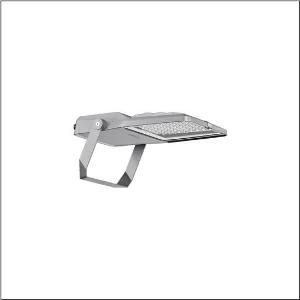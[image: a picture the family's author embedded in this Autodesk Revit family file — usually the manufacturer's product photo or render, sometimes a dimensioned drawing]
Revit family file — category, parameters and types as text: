
# Revit family: floodlight_fl_21_mini___pl64_5xa7776d2e1a_08ea
name_source: partatom
category: Lighting Fixtures
units: mm (PartAtom-declared; Revit-internal decimal feet)

## family parameters
Cut with Voids When Loaded = No
Host = Face
Light Source = No
Part Type = Normal
Room Calculation Point = No
Round Connector Dimension = Use Diameter
Shared = No

## types (1)
- --- (1 x LED, 17220 lm, 142.9 W, 3000K)
    Apparent Load = 143 VA
    CIE Flux Codes = 28 80 98 100 100
    Color Rendering = 70
    Color Temperature = 3000K
    Default Elevation = 1800 mm
    Description = Floodlight FL 21 mini, floodlight, primary light control with lens, of PMMA, primary optical cover: protective disc, of toughened safety glass, transparent, light distribution: PL64, light emission: direct distribution, installation type: surface-mounted, LED, High Power LED, rated luminous flux: 17.220lm, luminous efficacy: 121lm/W, light colour: 730, colour temperature: 3000K, control: flexible luminous flux parameterisation, time-dependent luminous flux control, constant luminous flux control, overheat protection, presetting dimming logarithmic, with terminal, 6-pole, mains connection: 220..240V, AC, 50/60Hz, start of lifetime: 143W, end of service life: 151W, reduction: 63W, luminaire housing, of diecast aluminium, powder-coated, Siteco® metallic grey (DB 702S), corrosivity category C5 mid according to DIN EN ISO 12944, sealing non-destructively replaceable, mounting bracket, of steel, galvanised, powder-coated, Siteco® metallic grey (DB 702S), Smart Interface below and above, protection rating (complete): IP66, insulation class (complete): insulation class II (safety insulation), certification: CE, ENEC, VDE, protection symbol: D, impact resistance: IK08, permissible operating ambient temperature: -40..+40°C, permissible operating ambient temperature for outdoor applications: -40..+50°C, standard: DIN EN 12944, LABS conformity tested according to VDMA 24364:2018-05, packaging unit: 1 piece

Light Distribution: PL64
    Height = 70 mm
    Lamp = 1 x LED
    Lamp Light Flux = 17220 lm
    Lamp Power = 142.9 W
    Lamp count = 1
    Length = 485 mm
    Luminous efficacy = 121 lm/W
    Manufacturer = Siteco
    ModVariant = No
    Model = 5XA7776D2E1A
    Number of Poles = 1
    OnlyDefault = Yes
    Power Factor = 1
    Product Name = Floodlight FL 21 mini | PL64
    Product group = floodlight | pylon annexe
    ProductGroupID = 6200
    Protection Class = Protection class II
    Protection Degree = IP 66
    RLX_Detail_Level = 1
    RLX_Emergency_Light_Flux = 0 lm
    RLX_Emergency_Type = 0
    RLX_Emergency_Type_DB = No
    RlxData = <blob elided: 96313 chars, md5=7f99710e>
    Socket = socket
    Standby Power = 0 W
    System Light Flux = 17220 lm
    System Power = 143 W
    Type Comments = factory setting: luminous flux: 100 % | dim-lin: 254 | 730 mA
    Type Image = l_1006845.jpg
    URL = http://relux.com
    VarID = @adj_097539
    Voltage = 0 V
    Weight = 0.00 kg
    Width = 337 mm

## geometry (parser evidence)
native form markers: Blend x4, Sweep x14
no freeform markers — native parametric forms only
